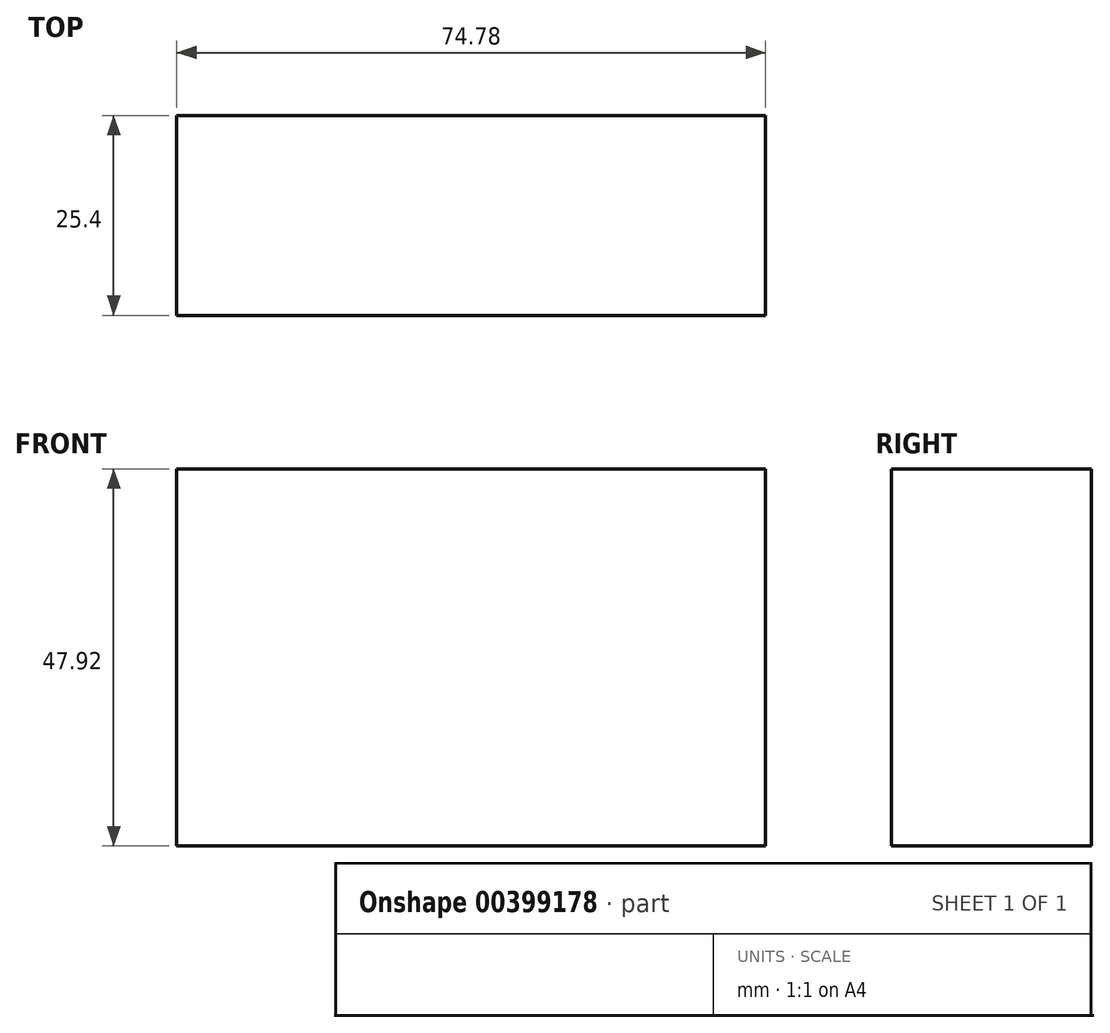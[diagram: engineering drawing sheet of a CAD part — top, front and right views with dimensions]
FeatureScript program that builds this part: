
annotation { "Feature Type Name" : "Feature", "Feature Type Description" : "" }
export const myFeature = defineFeature(function(context is Context, id is Id, definition is map)
    precondition{}
    {
        {
            var Q0;
            Q0=qCreatedBy(makeId("Front.planeOp"),FACE);
            var sketch = newSketch(context, id + "F0", { "sketchPlane" : qUnion([Q0])});
            skLineSegment(sketch, "E0.bottom", {"start": v(37.4, 23.96) * mm, "end": v(-37.4, 23.96) * mm});
            skLineSegment(sketch, "E0.top", {"start": v(37.4, -23.96) * mm, "end": v(-37.4, -23.96) * mm});
            skLineSegment(sketch, "E0.left", {"start": v(37.4, 23.96) * mm, "end": v(37.4, -23.96) * mm});
            skLineSegment(sketch, "E0.right", {"start": v(-37.4, 23.96) * mm, "end": v(-37.4, -23.96) * mm});
            skPoint(sketch, "E0.middle", {"position": v(0, 0) * mm});
            skSolve(sketch);
        }
        {
            var Q0;
            Q0=makeQuery(id+"F0.imprint","IMPRINT",FACE,{"disambiguationData":[TD([[makeQuery(id+"F0.imprint","IMPRINT",EDGE,{"derivedFrom":sQuery(id+"F0.wireOp",EDGE,"E0.bottom")}),1.0]])]});
            extrude(context, id + "F1", {"entities" : qUnion([Q0]), "depth" : 25.4 * mm});
        }
    });
